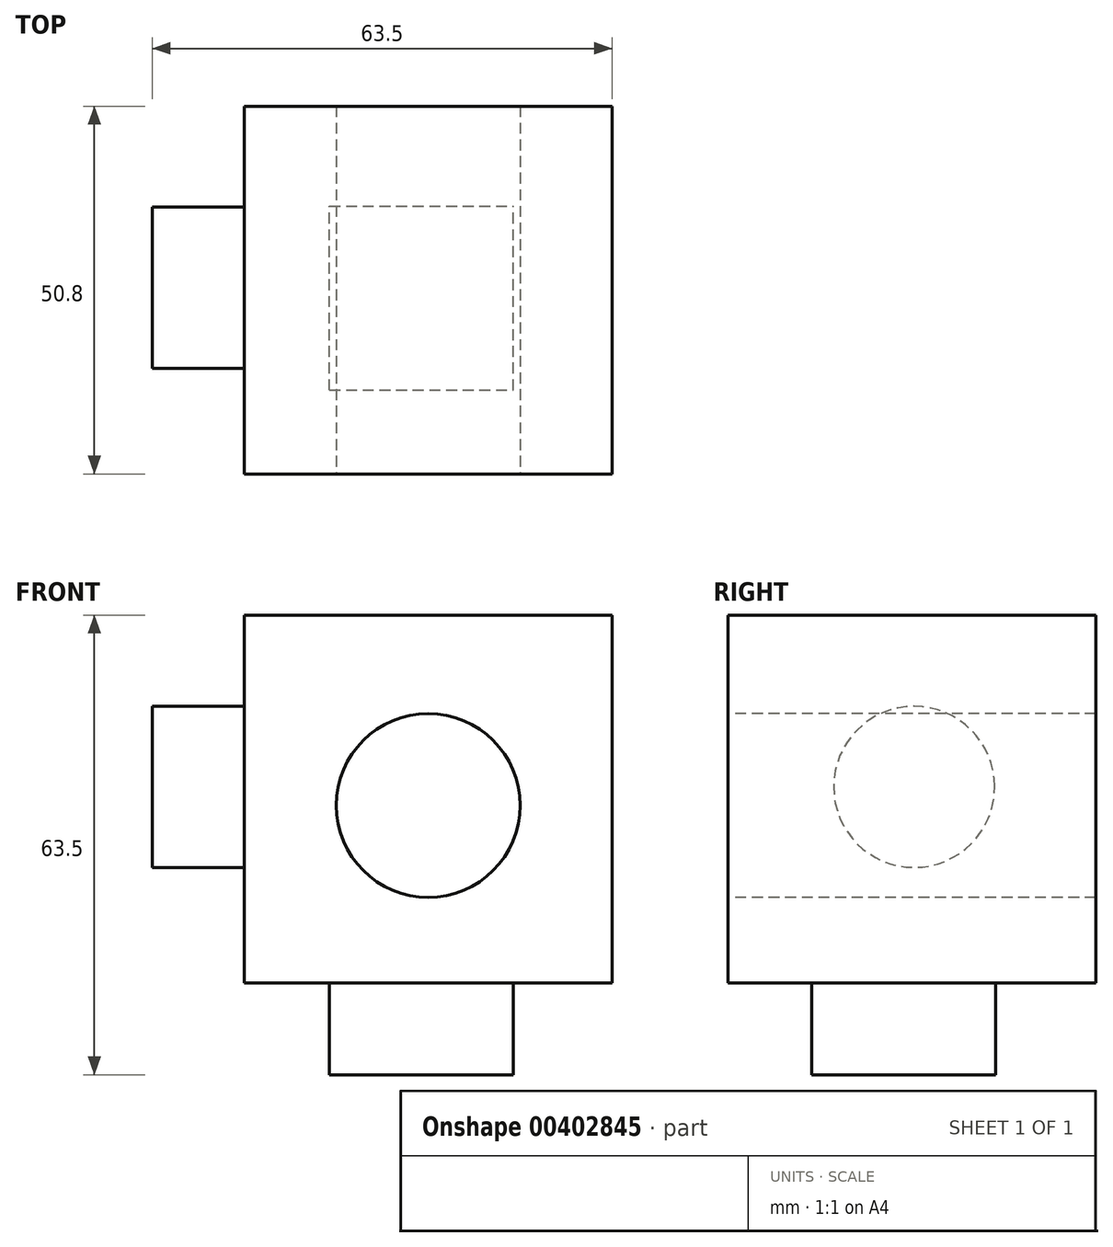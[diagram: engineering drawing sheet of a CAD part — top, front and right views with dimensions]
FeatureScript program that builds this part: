
annotation { "Feature Type Name" : "Feature", "Feature Type Description" : "" }
export const myFeature = defineFeature(function(context is Context, id is Id, definition is map)
    precondition{}
    {
        {
            var Q0;
            Q0=qCreatedBy(makeId("Front.planeOp"),FACE);
            var sketch = newSketch(context, id + "F0", { "sketchPlane" : qUnion([Q0])});
            skLineSegment(sketch, "E0", {"start": v(0, 0) * mm, "end": v(-25.4, 0) * mm});
            skLineSegment(sketch, "E1", {"start": v(0, 0) * mm, "end": v(25.4, 0) * mm});
            skLineSegment(sketch, "E2", {"start": v(-25.4, 0) * mm, "end": v(-25.4, 50.8) * mm});
            skLineSegment(sketch, "E3", {"start": v(-25.4, 50.8) * mm, "end": v(25.4, 50.8) * mm});
            skLineSegment(sketch, "E4", {"start": v(25.4, 50.8) * mm, "end": v(25.4, 0) * mm});
            skSolve(sketch);
        }
        {
            var Q0;
            Q0 = qSketchRegion(id + "F0", true);
            extrude(context, id + "F1", {"entities" : qUnion([Q0]), "depth" : 50.8 * mm});
        }
        {
            var Q0;
            Q0=makeQuery(id+"F1.opExtrude","CAP_FACE",FACE,{"disambiguationData":[OSD([sQuery(id+"F0.wireOp",EDGE,"E0"),sQuery(id+"F0.wireOp",EDGE,"E1"),sQuery(id+"F0.wireOp",EDGE,"E2"),sQuery(id+"F0.wireOp",EDGE,"E3"),sQuery(id+"F0.wireOp",EDGE,"E4")])],"isStart":false});
            var sketch = newSketch(context, id + "F2", { "sketchPlane" : qUnion([Q0])});
            skCircle(sketch, "E5", {"center": v(0, 24.5) * mm, "radius": 12.7 * mm});
            skSolve(sketch);
        }
        {
            var Q0;
            Q0=makeQuery(id+"F2.imprint","IMPRINT",FACE,{"disambiguationData":[TD([[makeQuery(id+"F2.imprint","IMPRINT",EDGE,{"derivedFrom":sQuery(id+"F2.wireOp",EDGE,"E5")}),1.0]])]});
            extrude(context, id + "F3", {"entities" : qUnion([Q0]), "operationType" : NewBodyOperationType.REMOVE, "oppositeDirection" : true, "depth" : 50.8 * mm});
        }
        {
            var Q0;
            Q0=makeQuery(id+"F1.opExtrude","SWEPT_FACE",FACE,{"disambiguationData":[OSD([sQuery(id+"F0.wireOp",EDGE,"E0"),sQuery(id+"F0.wireOp",EDGE,"E1")])]});
            var sketch = newSketch(context, id + "F4", { "sketchPlane" : qUnion([Q0])});
            skLineSegment(sketch, "E6", {"start": v(-13.63, 39.23) * mm, "end": v(-13.63, 13.83) * mm});
            skLineSegment(sketch, "E7", {"start": v(-13.63, 13.83) * mm, "end": v(11.77, 13.83) * mm});
            skLineSegment(sketch, "E8", {"start": v(11.77, 13.83) * mm, "end": v(12.25, 16.2) * mm});
            skLineSegment(sketch, "E9", {"start": v(-13.63, 39.23) * mm, "end": v(11.77, 39.23) * mm});
            skLineSegment(sketch, "E10", {"start": v(11.77, 39.23) * mm, "end": v(11.77, 13.83) * mm});
            skSolve(sketch);
        }
        {
            var Q0;
            Q0 = qSketchRegion(id + "F4", true);
            extrude(context, id + "F5", {"entities" : qUnion([Q0]), "operationType" : NewBodyOperationType.ADD, "depth" : 12.7 * mm});
        }
        {
            var Q0;
            Q0=makeQuery(id+"F1.opExtrude","SWEPT_FACE",FACE,{"disambiguationData":[OSD([sQuery(id+"F0.wireOp",EDGE,"E2")])]});
            var sketch = newSketch(context, id + "F6", { "sketchPlane" : qUnion([Q0])});
            skCircle(sketch, "E11", {"center": v(25.09, 27.07) * mm, "radius": 11.12 * mm});
            skSolve(sketch);
        }
        {
            var Q0;
            Q0=makeQuery(id+"F6.imprint","IMPRINT",FACE,{"disambiguationData":[TD([[makeQuery(id+"F6.imprint","IMPRINT",EDGE,{"derivedFrom":sQuery(id+"F6.wireOp",EDGE,"E11")}),1.0]])]});
            extrude(context, id + "F7", {"entities" : qUnion([Q0]), "operationType" : NewBodyOperationType.ADD, "depth" : 12.7 * mm});
        }
    });
